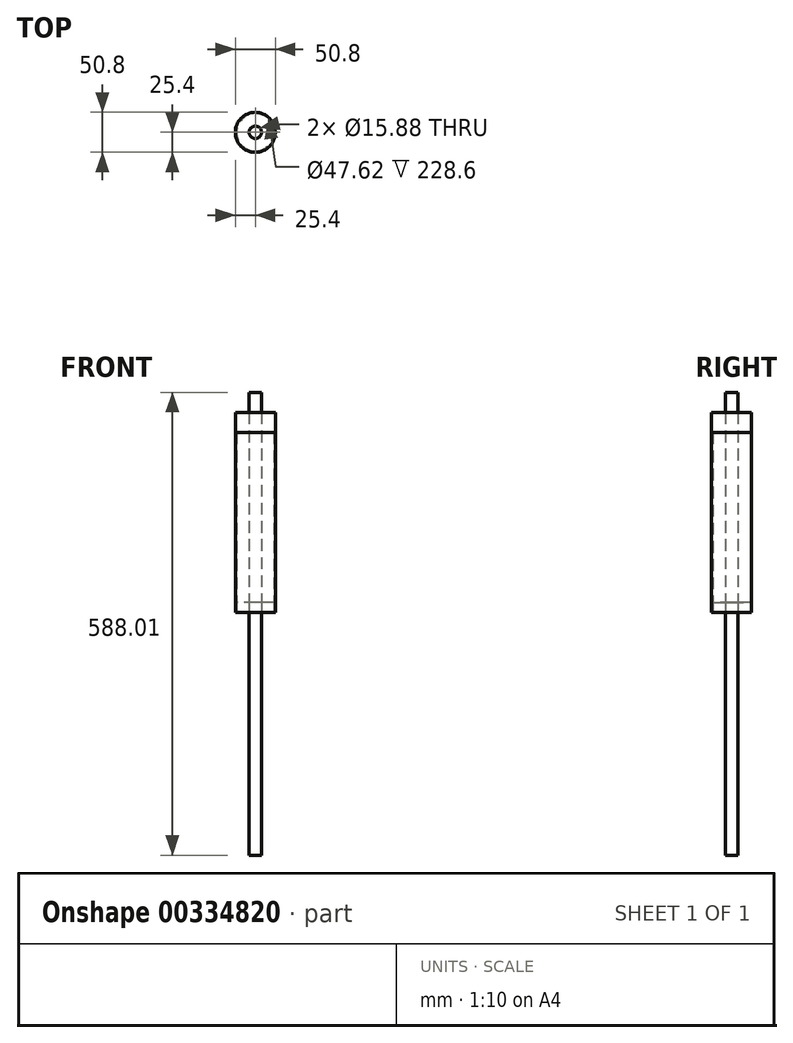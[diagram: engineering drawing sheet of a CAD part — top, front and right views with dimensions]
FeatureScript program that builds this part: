
annotation { "Feature Type Name" : "Feature", "Feature Type Description" : "" }
export const myFeature = defineFeature(function(context is Context, id is Id, definition is map)
    precondition{}
    {
        {
            var Q0;
            Q0=qCreatedBy(makeId("Top.planeOp"),FACE);
            var sketch = newSketch(context, id + "F0", { "sketchPlane" : qUnion([Q0])});
            skCircle(sketch, "E0", {"center": v(0, 0) * mm, "radius": 25.4 * mm});
            skCircle(sketch, "E1.0", {"center": v(0, 0) * mm, "radius": 23.81 * mm});
            skSolve(sketch);
        }
        {
            var Q0;
            Q0=qSketchRegion(id+"F0",true);
            extrude(context, id + "F1", {"entities" : qUnion([Q0]), "depth" : 228.6 * mm});
        }
        {
            var Q0;
            Q0=makeQuery(id+"F1.opExtrude","CAP_FACE",FACE,{"disambiguationData":[OSD([sQuery(id+"F0.wireOp",EDGE,"E0"),sQuery(id+"F0.wireOp",EDGE,"E1.0")])],"isStart":false});
            var sketch = newSketch(context, id + "F2", { "sketchPlane" : qUnion([Q0])});
            skCircle(sketch, "E2.0", {"center": v(0, 0) * mm, "radius": 25.4 * mm});
            skCircle(sketch, "E3", {"center": v(0, 0) * mm, "radius": 7.94 * mm});
            skSolve(sketch);
        }
        {
            var Q0;
            Q0=qSketchRegion(id+"F2",true);
            extrude(context, id + "F3", {"entities" : qUnion([Q0]), "depth" : 25.4 * mm});
        }
        {
            var Q0;
            Q0=qCreatedBy(makeId("Top.planeOp"),FACE);
            var sketch = newSketch(context, id + "F4", { "sketchPlane" : qUnion([Q0])});
            skCircle(sketch, "E4.0", {"center": v(0, 0) * mm, "radius": 23.81 * mm});
            skCircle(sketch, "E5.0", {"center": v(0, 0) * mm, "radius": 7.94 * mm});
            skSolve(sketch);
        }
        {
            var Q0;
            Q0=qSketchRegion(id+"F4",true);
            extrude(context, id + "F5", {"entities" : qUnion([Q0]), "depth" : 12.7 * mm});
        }
        {
            var Q0;
            Q0=makeQuery(id+"F5.opExtrude","CAP_FACE",FACE,{"disambiguationData":[OSD([sQuery(id+"F4.wireOp",EDGE,"E4.0"),sQuery(id+"F4.wireOp",EDGE,"E5.0")])],"isStart":true});
            var sketch = newSketch(context, id + "F6", { "sketchPlane" : qUnion([Q0])});
            skCircle(sketch, "E6.0", {"center": v(0, 0) * mm, "radius": 7.94 * mm});
            skSolve(sketch);
        }
        {
            var Q0;
            Q0=qSketchRegion(id+"F6",true);
            extrude(context, id + "F7", {"entities" : qUnion([Q0]), "oppositeDirection" : true, "depth" : 279.4 * mm});
        }
        {
            var Q0;
            Q0=makeQuery(id+"F7.opExtrude","CAP_FACE",FACE,{"disambiguationData":[OSD([sQuery(id+"F6.wireOp",EDGE,"E6.0")])],"isStart":true});
            var sketch = newSketch(context, id + "F8", { "sketchPlane" : qUnion([Q0])});
            skCircle(sketch, "E7.0", {"center": v(0, 0) * mm, "radius": 7.94 * mm});
            skSolve(sketch);
        }
        {
            var Q0;
            Q0=qSketchRegion(id+"F8",true);
            extrude(context, id + "F9", {"entities" : qUnion([Q0]), "depth" : 308.6 * mm});
        }
    });
